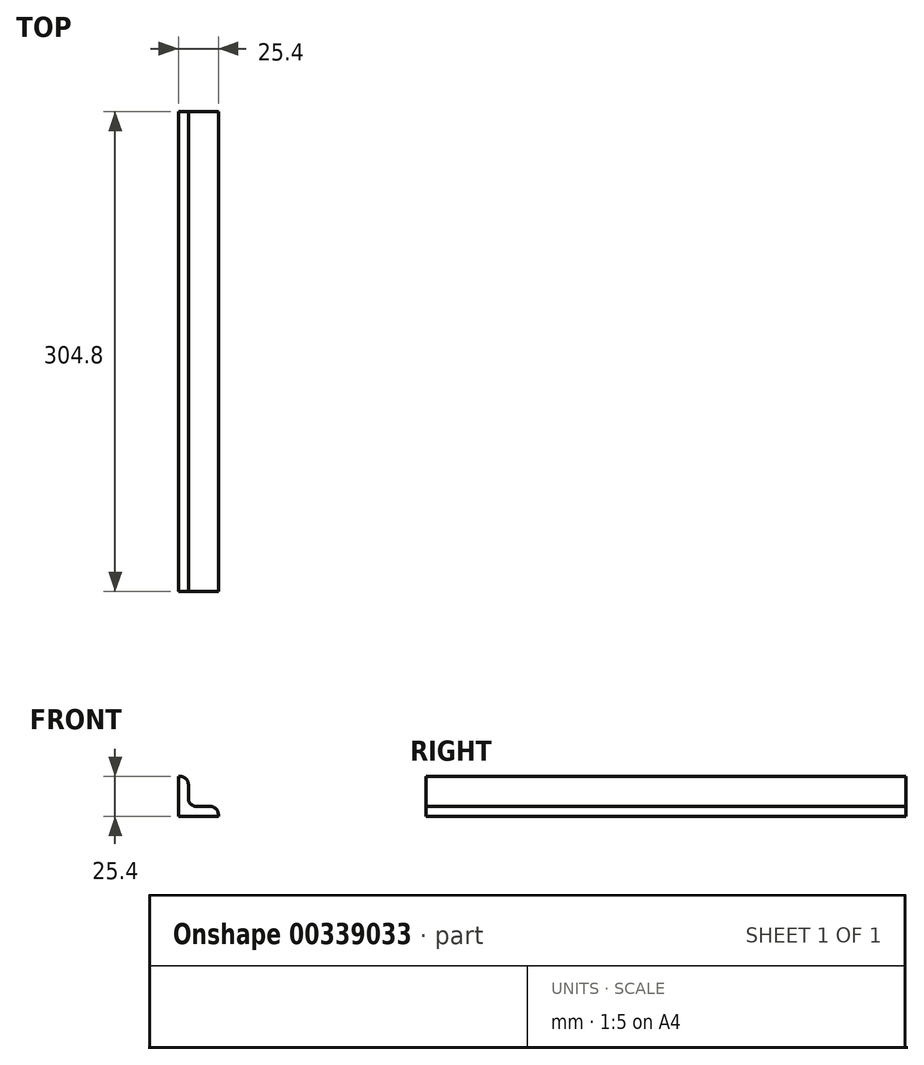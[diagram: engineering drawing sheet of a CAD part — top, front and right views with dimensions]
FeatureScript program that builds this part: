
annotation { "Feature Type Name" : "Feature", "Feature Type Description" : "" }
export const myFeature = defineFeature(function(context is Context, id is Id, definition is map)
    precondition{}
    {
        {
            var Q0;
            Q0=qCreatedBy(makeId("Front.planeOp"),FACE);
            var sketch = newSketch(context, id + "F0", { "sketchPlane" : qUnion([Q0])});
            skLineSegment(sketch, "E0", {"start": v(0, 0) * mm, "end": v(25.4, 0) * mm});
            skLineSegment(sketch, "E1", {"start": v(0, 0) * mm, "end": v(0, 25.4) * mm});
            skLineSegment(sketch, "E2.0", {"start": v(6.35, 11.43) * mm, "end": v(6.35, 20.32) * mm});
            skLineSegment(sketch, "E3.0", {"start": v(11.43, 6.35) * mm, "end": v(20.32, 6.35) * mm});
            skLineSegment(sketch, "E4.0", {"start": v(0, 25.4) * mm, "end": v(1.27, 25.4) * mm});
            skLineSegment(sketch, "E5.0", {"start": v(25.4, 0) * mm, "end": v(25.4, 1.27) * mm});
            skArc(sketch, "E6.filletArc", {"start": v(6.35, 20.32) * mm, "mid": v(4.86, 23.91) * mm, "end": v(1.27, 25.4) * mm});
            skArc(sketch, "E7.filletArc", {"start": v(6.35, 11.43) * mm, "mid": v(7.84, 7.84) * mm, "end": v(11.43, 6.35) * mm});
            skArc(sketch, "E8.filletArc", {"start": v(25.4, 1.27) * mm, "mid": v(23.91, 4.86) * mm, "end": v(20.32, 6.35) * mm});
            skSolve(sketch);
        }
        {
            var Q0;
            Q0 = qSketchRegion(id + "F0", true);
            extrude(context, id + "F1", {"entities" : qUnion([Q0]), "depth" : 304.8 * mm});
        }
    });
